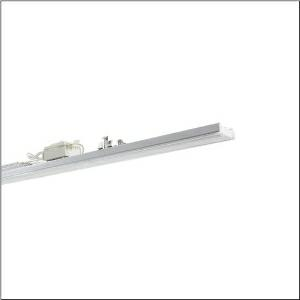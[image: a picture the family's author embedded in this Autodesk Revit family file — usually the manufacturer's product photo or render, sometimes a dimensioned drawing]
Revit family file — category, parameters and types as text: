
# Revit family: licross_r__21_recessed_mo_52tl10dv4e5g_ca6c
name_source: partatom
category: Lighting Fixtures
units: mm (PartAtom-declared; Revit-internal decimal feet)

## family parameters
Cut with Voids When Loaded = No
Host = Face
Light Source = No
Part Type = Normal
Room Calculation Point = No
Round Connector Dimension = Use Diameter
Shared = No

## types (1)
- --- (1 x LED, 14990 lm, 85.3 W, 4000K)
    Apparent Load = 85 VA
    CIE Flux Codes = 50 81 96 100 100
    Color Rendering = 80
    Color Temperature = 4000K
    Default Elevation = 1800 mm
    Description = Licross® 21 Recessed MO, luminaire insert, of sheet steel, galvanised, coil coated, white, length: 2.250mm, width: 66mm, height: 67mm, LED rated luminous flux: 14.990lm, light colour: 840, control gear: DALI 2, with plug, 5-pole, with phase selection, mains connection: 220..240V, AC, 50/60Hz, rated input power: 85W, halogen-free wiring, primary optical cover: cover, of PMMA, light emission: direct distribution, primary light characteristic: symmetric, protection rating (complete): IP40, insulation class (complete): insulation class I (protective earthing), certification: CE, ENEC, VDE, UKCA, protection symbol: D if used in an environment without relevant dust loads with corresponding accessories, impact resistance: IK06, permissible ambient temperature for indoor applications: -25..+35°C, corresponds to IFS (International Featured Standards) requirements for safety and quality in the food industry, reducing of maximum allowable ambient temperature of 5°C with ceiling mounting, LABS conformity tested according to VDMA 24364:2018-05, packaging unit: 1 piece
    Height = 58 mm
    Lamp = 1 x LED
    Lamp Light Flux = 14990 lm
    Lamp Power = 85.3 W
    Lamp count = 1
    Length = 2250 mm
    Luminous efficacy = 176 lm/W
    Manufacturer = Siteco
    ModVariant = No
    Model = 52TL10DV4E5G
    Mounting Place = Ceiling
    Mounting Type = Pendant
    Number of Poles = 1
    OnlyDefault = Yes
    Power Factor = 1
    Product Name = Licross® 21 Recessed MO
    Product group = luminaire insert
    ProductGroupID = 902
    Protection Class = Protection class I
    Protection Degree = IP 40
    RLX_Detail_Level = 1
    RLX_Emergency_Light_Flux = 0 lm
    RLX_Emergency_Type = 0
    RLX_Emergency_Type_DB = No
    RlxData = <blob elided: 29193 chars, md5=77a24dbb>
    Socket = socket
    Standby Power = 0 W
    System Light Flux = 14990 lm
    System Power = 85 W
    Type Comments = factory setting: luminous flux: 100 % | dim-lin: 254 | 390 mA
    Type Image = l_1296930.jpg
    URL = http://relux.com
    VarID = @adj_127634
    Voltage = 0 V
    Weight = 0.00 kg
    Width = 66 mm

## geometry (parser evidence)
native form markers: Blend x4, Sweep x10
no freeform markers — native parametric forms only
